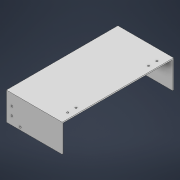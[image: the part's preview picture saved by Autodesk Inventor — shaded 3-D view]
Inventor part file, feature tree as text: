
AUTODESK INVENTOR PART (.ipt)
format: ipt  version: 2021 (Build 250183000, 183)  size: 297,984 bytes
history: native  units: mm
features: extrude x7, sketch x7, other x1
ambient origin geometry x8: Origin, YZ Plane, XZ Plane, XY Plane, X Axis, Y Axis, Z Axis, Center Point
bodies: Volumenkörper1 (feature_tree)
feature tree (15):
  other  "Ebene3_mitte_vorne"
  extrude  "Extrusion1"  Depth=200.0mm
  extrude  "Extrusion3"  Depth=2.0mm
  extrude  "Extrusion4"  Depth=48.0mm TaperAngle=0.0deg
  extrude  "Extrusion5"  Depth=3.2mm
  extrude  "Extrusion6"  Depth=15.0mm
  extrude  "Extrusion7"  Depth=10.0mm
  extrude  "Extrusion8"  Depth=50.0mm
  sketch  "Skizze1"  dims[d0=100.0mm d1=200.0mm]
  sketch  "Skizze3"  dims[d2=2.0mm d3=0.0mm d8=2.0mm]
  sketch  "Skizze4"  dims[d9=2.0mm d10=48.0mm d11=0.0mm]
  sketch  "Skizze5"  dims[d12=3.2mm d13=3.2mm]
  sketch  "Skizze6"  dims[d14=15.0mm d15=15.0mm]
  sketch  "Skizze7"  dims[d16=10.0mm d17=10.0mm]
  sketch  "Skizze8"  dims[d18=50.0mm d19=0.0mm d20=3.2mm d21=3.2mm d22=10.0mm d23=10.0mm d24=15.0mm d25=15.0mm d26=50.0mm d27=0.0mm d31=3.2mm d32=3.2mm d33=3.2mm d34=3.2mm d35=10.0mm d36=10.0mm d37=15.0mm d38=10.0mm d39=10.0mm d40=15.0mm d41=20.0mm d42=20.0mm d43=2.0mm d44=0.0mm d45=3.2mm d46=25.0mm d47=5.0mm d48=2.0mm d49=0.0mm d50=3.2mm d51=25.0mm d52=5.0mm d53=50.0mm d54=0.0mm]
